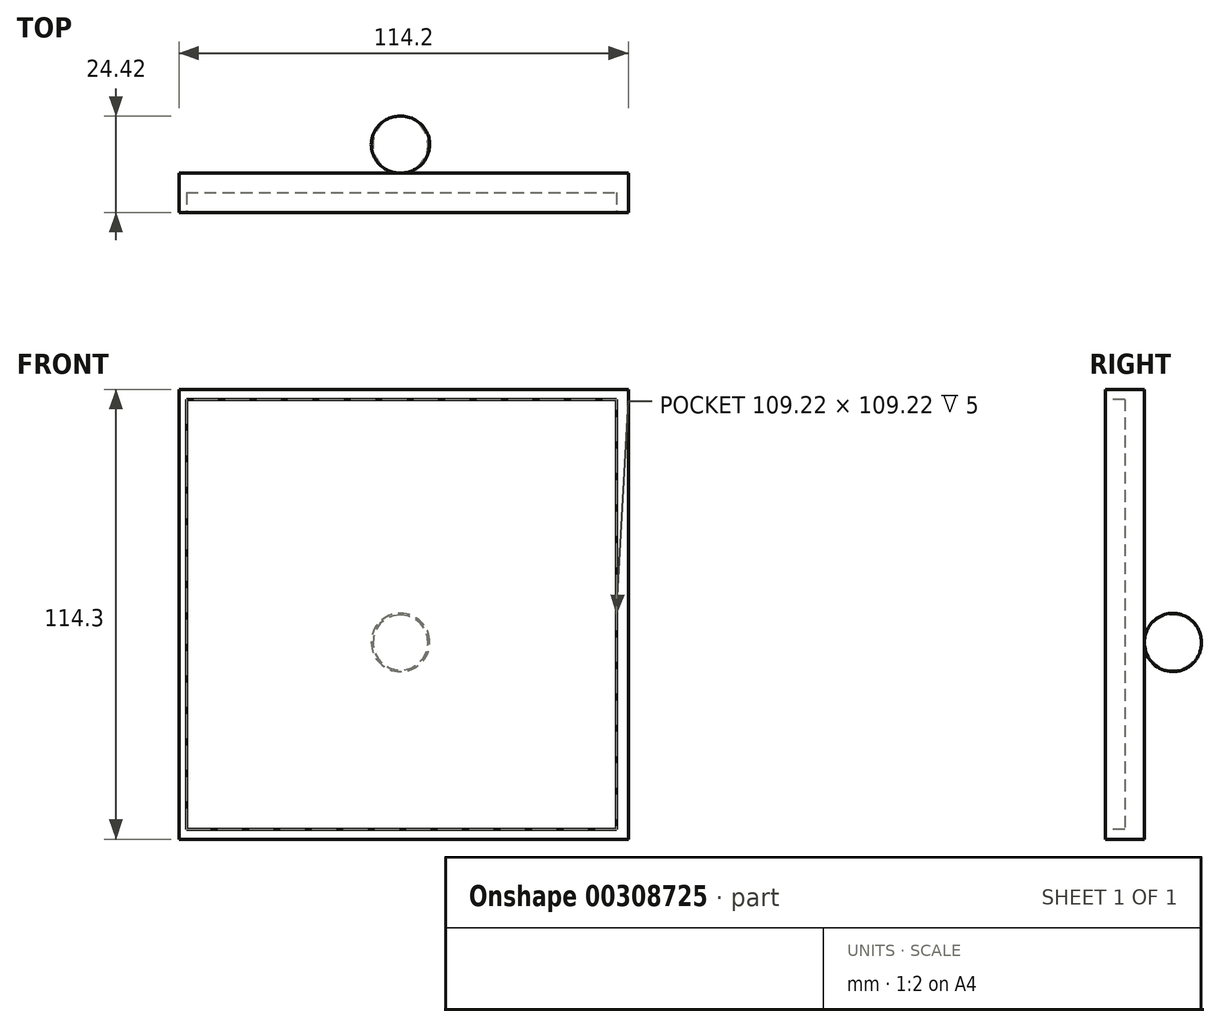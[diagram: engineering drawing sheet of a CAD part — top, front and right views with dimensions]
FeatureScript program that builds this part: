
annotation { "Feature Type Name" : "Feature", "Feature Type Description" : "" }
export const myFeature = defineFeature(function(context is Context, id is Id, definition is map)
    precondition{}
    {
        {
            var Q0;
            Q0=qCreatedBy(makeId("Front.planeOp"),FACE);
            var sketch = newSketch(context, id + "F0", { "sketchPlane" : qUnion([Q0])});
            skLineSegment(sketch, "E0.bottom", {"start": v(-45.35, 64.3) * mm, "end": v(68.85, 64.3) * mm});
            skLineSegment(sketch, "E0.top", {"start": v(-45.35, -50) * mm, "end": v(68.85, -50) * mm});
            skLineSegment(sketch, "E0.left", {"start": v(-45.35, 64.3) * mm, "end": v(-45.35, -50) * mm});
            skLineSegment(sketch, "E0.right", {"start": v(68.85, 64.3) * mm, "end": v(68.85, -50) * mm});
            skSolve(sketch);
        }
        {
            var Q0;
            Q0 = qSketchRegion(id + "F0", true);
            extrude(context, id + "F1", {"entities" : qUnion([Q0]), "depth" : 10 * mm});
        }
        {
            var Q0;
            Q0=makeQuery(id+"F1.opExtrude","CAP_FACE",FACE,{"disambiguationData":[OSD([sQuery(id+"F0.wireOp",EDGE,"E0.bottom"),sQuery(id+"F0.wireOp",EDGE,"E0.top"),sQuery(id+"F0.wireOp",EDGE,"E0.left"),sQuery(id+"F0.wireOp",EDGE,"E0.right")])],"isStart":false});
            var sketch = newSketch(context, id + "F2", { "sketchPlane" : qUnion([Q0])});
            skLineSegment(sketch, "E1.bottom", {"start": v(-43.45, 61.75) * mm, "end": v(65.77, 61.75) * mm});
            skLineSegment(sketch, "E1.top", {"start": v(-43.45, -47.47) * mm, "end": v(65.77, -47.47) * mm});
            skLineSegment(sketch, "E1.left", {"start": v(-43.45, 61.75) * mm, "end": v(-43.45, -47.47) * mm});
            skLineSegment(sketch, "E1.right", {"start": v(65.77, 61.75) * mm, "end": v(65.77, -47.47) * mm});
            skSolve(sketch);
        }
        {
            var Q0;
            Q0 = qSketchRegion(id + "F2", true);
            extrude(context, id + "F3", {"entities" : qUnion([Q0]), "operationType" : NewBodyOperationType.REMOVE, "oppositeDirection" : true, "depth" : 5 * mm});
        }
        {
            var Q0;
            Q0=qCreatedBy(makeId("Top.planeOp"),FACE);
            var sketch = newSketch(context, id + "F4", { "sketchPlane" : qUnion([Q0])});
            skLineSegment(sketch, "E2", {"start": v(10.93, 0) * mm, "end": v(10.93, 14.42) * mm});
            skArc(sketch, "E3", {"start": v(10.93, 0) * mm, "mid": v(17.95, 7.21) * mm, "end": v(10.93, 14.42) * mm});
            skSolve(sketch);
        }
        {
            var Q0;
            Q0 = qSketchRegion(id + "F4", true);
            var Q1;
            Q1=sQuery(id+"F4.wireOp",EDGE,"E2");
            revolve(context, id + "F5", {"entities" : qUnion([Q0]), "axis" : qUnion([Q1]), "revolveType" : RevolveType.FULL});
        }
    });
